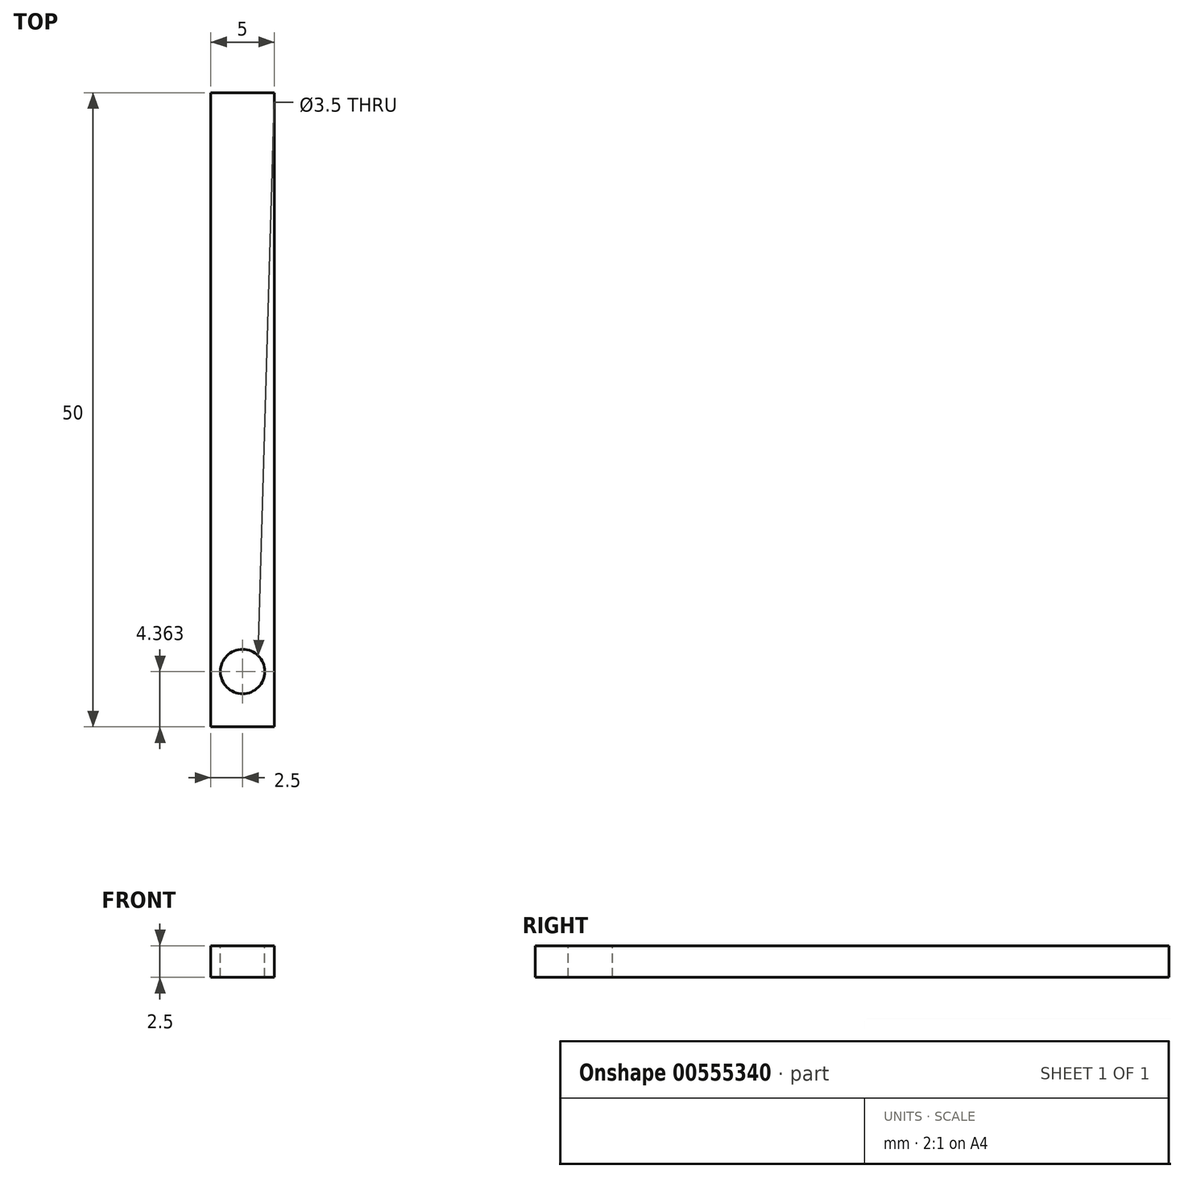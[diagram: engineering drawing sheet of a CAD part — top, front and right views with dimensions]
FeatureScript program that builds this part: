
annotation { "Feature Type Name" : "Feature", "Feature Type Description" : "" }
export const myFeature = defineFeature(function(context is Context, id is Id, definition is map)
    precondition{}
    {
        {
            var Q0;
            Q0=qCreatedBy(makeId("Front.planeOp"),FACE);
            var sketch = newSketch(context, id + "F0", { "sketchPlane" : qUnion([Q0])});
            skLineSegment(sketch, "E0.bottom", {"start": v(0, 0) * mm, "end": v(5, 0) * mm});
            skLineSegment(sketch, "E0.top", {"start": v(0, -2.5) * mm, "end": v(5, -2.5) * mm});
            skLineSegment(sketch, "E0.left", {"start": v(0, 0) * mm, "end": v(0, -2.5) * mm});
            skLineSegment(sketch, "E0.right", {"start": v(5, 0) * mm, "end": v(5, -2.5) * mm});
            skSolve(sketch);
        }
        {
            var Q0;
            Q0 = qSketchRegion(id + "F0", true);
            extrude(context, id + "F1", {"entities" : qUnion([Q0]), "depth" : 50 * mm, "offsetDistance" : 25 * mm});
        }
        {
            var Q0;
            Q0=makeQuery(id+"F1.opExtrude","SWEPT_FACE",FACE,{"disambiguationData":[OSD([sQuery(id+"F0.wireOp",EDGE,"E0.bottom")])]});
            var sketch = newSketch(context, id + "F2", { "sketchPlane" : qUnion([Q0])});
            skCircle(sketch, "E1", {"center": v(2.5, -45.64) * mm, "radius": 1.75 * mm});
            skPoint(sketch, "E1.centerSnap0", {"position": v(2.5, 0) * mm});
            skSolve(sketch);
        }
        {
            var Q0;
            Q0 = qSketchRegion(id + "F2", true);
            extrude(context, id + "F3", {"entities" : qUnion([Q0]), "operationType" : NewBodyOperationType.REMOVE, "oppositeDirection" : true, "depth" : 25 * mm, "offsetDistance" : 25 * mm});
        }
    });
